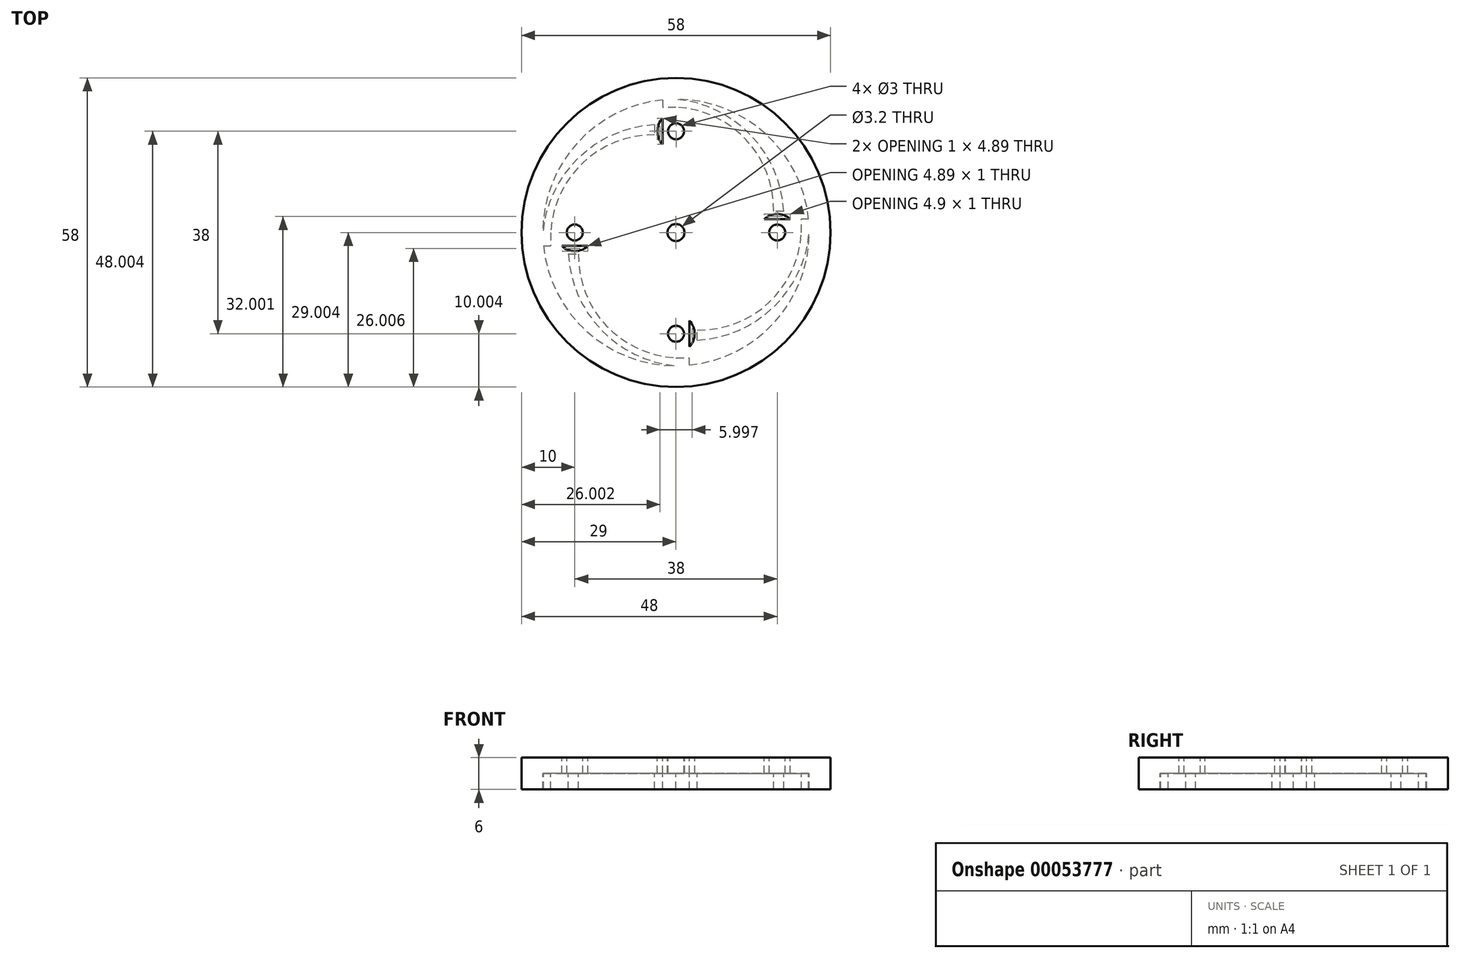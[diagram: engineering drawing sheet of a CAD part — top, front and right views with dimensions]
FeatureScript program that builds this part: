
annotation { "Feature Type Name" : "Feature", "Feature Type Description" : "" }
export const myFeature = defineFeature(function(context is Context, id is Id, definition is map)
    precondition{}
    {
        {
            var Q0;
            Q0=qCreatedBy(makeId("Top.planeOp"),FACE);
            var sketch = newSketch(context, id + "F0", { "sketchPlane" : qUnion([Q0])});
            skCircle(sketch, "E0", {"center": v(0, -6.1) * mm, "radius": 1.6 * mm});
            skCircle(sketch, "E1", {"center": v(0, -6.1) * mm, "radius": 25 * mm});
            skCircle(sketch, "E2", {"center": v(0, -6.1) * mm, "radius": 29 * mm});
            skLineSegment(sketch, "E3", {"start": v(-25, -6.1) * mm, "end": v(25, -6.1) * mm, "construction": true});
            skLineSegment(sketch, "E4", {"start": v(0, 18.9) * mm, "end": v(0, -31.1) * mm, "construction": true});
            skLineSegment(sketch, "E5", {"start": v(0, 13.94) * mm, "end": v(0, 11.74) * mm, "construction": true});
            skLineSegment(sketch, "E6", {"start": v(0, 11.74) * mm, "end": v(0, 13.94) * mm, "construction": true});
            skPoint(sketch, "E7", {"position": v(-23.5, -6.1) * mm});
            skArc(sketch, "E8", {"start": v(-4, 14.1) * mm, "mid": v(-18.27, 7.91) * mm, "end": v(-25, -6.1) * mm});
            skArc(sketch, "E9", {"start": v(-4, 12.22) * mm, "mid": v(-17.46, 7) * mm, "end": v(-23.5, -6.1) * mm});
            skLineSegment(sketch, "E10", {"start": v(-25, -6.1) * mm, "end": v(-23.5, -6.1) * mm});
            skLineSegment(sketch, "E11", {"start": v(-4, 14.1) * mm, "end": v(-4, 12.22) * mm});
            skLineSegment(sketch, "E12.1.0", {"start": v(-20.2, -10.1) * mm, "end": v(-18.33, -10.1) * mm});
            skArc(sketch, "E12.1.1", {"start": v(-20.2, -10.1) * mm, "mid": v(-14.02, -24.38) * mm, "end": v(0, -31.1) * mm});
            skArc(sketch, "E12.1.2", {"start": v(-18.33, -10.1) * mm, "mid": v(-13.1, -23.56) * mm, "end": v(0, -29.6) * mm});
            skLineSegment(sketch, "E12.1.3", {"start": v(0, -31.1) * mm, "end": v(0, -29.6) * mm});
            skLineSegment(sketch, "E12.2.0", {"start": v(4, -26.3) * mm, "end": v(4, -24.43) * mm});
            skArc(sketch, "E12.2.1", {"start": v(4, -26.3) * mm, "mid": v(18.27, -20.13) * mm, "end": v(25, -6.1) * mm});
            skArc(sketch, "E12.2.2", {"start": v(4, -24.43) * mm, "mid": v(17.46, -19.21) * mm, "end": v(23.5, -6.1) * mm});
            skLineSegment(sketch, "E12.2.3", {"start": v(25, -6.1) * mm, "end": v(23.5, -6.1) * mm});
            skLineSegment(sketch, "E12.3.0", {"start": v(20.2, -2.1) * mm, "end": v(18.33, -2.1) * mm});
            skArc(sketch, "E12.3.1", {"start": v(20.2, -2.1) * mm, "mid": v(14.02, 12.16) * mm, "end": v(0, 18.9) * mm});
            skArc(sketch, "E12.3.2", {"start": v(18.33, -2.1) * mm, "mid": v(13.1, 11.35) * mm, "end": v(0, 17.4) * mm});
            skLineSegment(sketch, "E12.3.3", {"start": v(0, 18.9) * mm, "end": v(0, 17.4) * mm});
            skLineSegment(sketch, "E13", {"start": v(-2.5, 18.77) * mm, "end": v(-2.5, -3.6) * mm});
            skLineSegment(sketch, "E14", {"start": v(2.5, -30.98) * mm, "end": v(2.5, -8.6) * mm});
            skLineSegment(sketch, "E15", {"start": v(-24.87, -8.6) * mm, "end": v(-2.5, -8.6) * mm});
            skLineSegment(sketch, "E16", {"start": v(24.88, -3.6) * mm, "end": v(2.5, -3.6) * mm});
            skPoint(sketch, "E17", {"position": v(2.5, -8.6) * mm});
            skPoint(sketch, "E18", {"position": v(2.5, -3.6) * mm});
            skPoint(sketch, "E19", {"position": v(-2.5, -3.6) * mm});
            skPoint(sketch, "E20", {"position": v(-2.5, -8.6) * mm});
            skLineSegment(sketch, "E21.trimOffspring", {"start": v(2.5, -8.6) * mm, "end": v(23.22, -8.6) * mm});
            skLineSegment(sketch, "E22.trimOffspring", {"start": v(-2.5, -8.6) * mm, "end": v(-2.5, -29.32) * mm});
            skLineSegment(sketch, "E23.trimOffspring", {"start": v(2.5, -3.6) * mm, "end": v(2.5, 17.11) * mm});
            skLineSegment(sketch, "E24.trimOffspring", {"start": v(-2.5, -3.6) * mm, "end": v(-23.22, -3.6) * mm});
            skLineSegment(sketch, "E25", {"start": v(23.5, -6.1) * mm, "end": v(23.5, -3.6) * mm});
            skLineSegment(sketch, "E26", {"start": v(0, 17.4) * mm, "end": v(-2.5, 17.4) * mm});
            skLineSegment(sketch, "E27", {"start": v(-23.5, -6.1) * mm, "end": v(-23.5, -8.6) * mm});
            skLineSegment(sketch, "E28", {"start": v(0, -29.6) * mm, "end": v(2.5, -29.6) * mm});
            skCircle(sketch, "E29", {"center": v(19, -6.1) * mm, "radius": 1.5 * mm});
            skCircle(sketch, "E30.1.0", {"center": v(0, 12.9) * mm, "radius": 1.5 * mm});
            skCircle(sketch, "E30.2.0", {"center": v(-19, -6.1) * mm, "radius": 1.5 * mm});
            skCircle(sketch, "E30.3.0", {"center": v(0, -25.1) * mm, "radius": 1.5 * mm});
            skCircle(sketch, "E31", {"center": v(-19, -6.1) * mm, "radius": 3.5 * mm});
            skCircle(sketch, "E32.1.0", {"center": v(0, -25.1) * mm, "radius": 3.5 * mm});
            skCircle(sketch, "E32.2.0", {"center": v(19, -6.1) * mm, "radius": 3.5 * mm});
            skCircle(sketch, "E32.3.0", {"center": v(0, 12.9) * mm, "radius": 3.5 * mm});
            skSolve(sketch);
        }
        {
            var Q0;
            Q0=makeQuery(id+"F0.imprint","IMPRINT",FACE,{"disambiguationData":[TD([[makeQuery(id+"F0.imprint","IMPRINT",EDGE,{"derivedFrom":sQuery(id+"F0.wireOp",EDGE,"E0")}),-1.0]])]});
            var Q1;
            {var subQ0=sQuery(id+"F0.wireOp",EDGE,"E31");var subQ1=sQuery(id+"F0.wireOp",EDGE,"E15");var subQ2=makeQuery(id+"F0.imprint","INTERSECT",VERTEX,{"disambiguationData":[OD(0.0)],"derivedFrom":[subQ1,subQ0]});Q1=makeQuery(id+"F0.imprint","IMPRINT",FACE,{"disambiguationData":[TD([[makeQuery(id+"F0.imprint","IMPRINT",EDGE,{"disambiguationData":[TD([[subQ2,-1.0]])],"derivedFrom":subQ1}),-1.0]])]});}
            var Q2;
            {var subQ0=sQuery(id+"F0.wireOp",EDGE,"E31");var subQ1=sQuery(id+"F0.wireOp",EDGE,"E24.trimOffspring");var subQ2=makeQuery(id+"F0.imprint","INTERSECT",VERTEX,{"disambiguationData":[OD(0.0)],"derivedFrom":[subQ1,subQ0]});Q2=makeQuery(id+"F0.imprint","IMPRINT",FACE,{"disambiguationData":[TD([[makeQuery(id+"F0.imprint","IMPRINT",EDGE,{"disambiguationData":[TD([[subQ2,-1.0]])],"derivedFrom":subQ1}),-1.0]])]});}
            var Q3;
            Q3=makeQuery(id+"F0.imprint","IMPRINT",FACE,{"disambiguationData":[TD([[makeQuery(id+"F0.imprint","IMPRINT",EDGE,{"derivedFrom":sQuery(id+"F0.wireOp",EDGE,"E30.2.0")}),-1.0]])]});
            var Q4;
            {var subQ0=sQuery(id+"F0.wireOp",EDGE,"E27");Q4=makeQuery(id+"F0.imprint","IMPRINT",FACE,{"disambiguationData":[TD([[makeQuery(id+"F0.imprint","IMPRINT",EDGE,{"derivedFrom":subQ0}),1.0]])]});}
            var Q5;
            {var subQ5=sQuery(id+"F0.wireOp",EDGE,"E26");Q5=makeQuery(id+"F0.imprint","IMPRINT",FACE,{"disambiguationData":[TD([[makeQuery(id+"F0.imprint","IMPRINT",EDGE,{"derivedFrom":subQ5}),1.0]])]});}
            var Q6;
            {var subQ0=sQuery(id+"F0.wireOp",EDGE,"E32.3.0");var subQ1=sQuery(id+"F0.wireOp",EDGE,"E13");var subQ2=makeQuery(id+"F0.imprint","INTERSECT",VERTEX,{"disambiguationData":[OD(0.0)],"derivedFrom":[subQ1,subQ0]});Q6=makeQuery(id+"F0.imprint","IMPRINT",FACE,{"disambiguationData":[TD([[makeQuery(id+"F0.imprint","IMPRINT",EDGE,{"disambiguationData":[TD([[subQ2,-1.0]])],"derivedFrom":subQ1}),-1.0]])]});}
            var Q7;
            Q7=makeQuery(id+"F0.imprint","IMPRINT",FACE,{"disambiguationData":[TD([[makeQuery(id+"F0.imprint","IMPRINT",EDGE,{"derivedFrom":sQuery(id+"F0.wireOp",EDGE,"E30.1.0")}),-1.0]])]});
            var Q8;
            {var subQ0=sQuery(id+"F0.wireOp",EDGE,"E32.3.0");var subQ1=sQuery(id+"F0.wireOp",EDGE,"E23.trimOffspring");var subQ2=makeQuery(id+"F0.imprint","INTERSECT",VERTEX,{"disambiguationData":[OD(0.0)],"derivedFrom":[subQ1,subQ0]});Q8=makeQuery(id+"F0.imprint","IMPRINT",FACE,{"disambiguationData":[TD([[makeQuery(id+"F0.imprint","IMPRINT",EDGE,{"disambiguationData":[TD([[subQ2,-1.0]])],"derivedFrom":subQ1}),-1.0]])]});}
            var Q9;
            Q9=makeQuery(id+"F0.imprint","IMPRINT",FACE,{"disambiguationData":[TD([[makeQuery(id+"F0.imprint","IMPRINT",EDGE,{"derivedFrom":sQuery(id+"F0.wireOp",EDGE,"E29")}),-1.0]])]});
            var Q10;
            {var subQ0=sQuery(id+"F0.wireOp",EDGE,"E25");Q10=makeQuery(id+"F0.imprint","IMPRINT",FACE,{"disambiguationData":[TD([[makeQuery(id+"F0.imprint","IMPRINT",EDGE,{"derivedFrom":subQ0}),1.0]])]});}
            var Q11;
            {var subQ0=sQuery(id+"F0.wireOp",EDGE,"E32.2.0");var subQ1=sQuery(id+"F0.wireOp",EDGE,"E21.trimOffspring");var subQ2=makeQuery(id+"F0.imprint","INTERSECT",VERTEX,{"disambiguationData":[OD(0.0)],"derivedFrom":[subQ1,subQ0]});Q11=makeQuery(id+"F0.imprint","IMPRINT",FACE,{"disambiguationData":[TD([[makeQuery(id+"F0.imprint","IMPRINT",EDGE,{"disambiguationData":[TD([[subQ2,-1.0]])],"derivedFrom":subQ1}),-1.0]])]});}
            var Q12;
            {var subQ0=sQuery(id+"F0.wireOp",EDGE,"E32.2.0");var subQ1=sQuery(id+"F0.wireOp",EDGE,"E16");var subQ2=makeQuery(id+"F0.imprint","INTERSECT",VERTEX,{"disambiguationData":[OD(0.0)],"derivedFrom":[subQ1,subQ0]});Q12=makeQuery(id+"F0.imprint","IMPRINT",FACE,{"disambiguationData":[TD([[makeQuery(id+"F0.imprint","IMPRINT",EDGE,{"disambiguationData":[TD([[subQ2,-1.0]])],"derivedFrom":subQ1}),-1.0]])]});}
            var Q13;
            Q13=makeQuery(id+"F0.imprint","IMPRINT",FACE,{"disambiguationData":[TD([[makeQuery(id+"F0.imprint","IMPRINT",EDGE,{"derivedFrom":sQuery(id+"F0.wireOp",EDGE,"E30.3.0")}),-1.0]])]});
            var Q14;
            {var subQ0=sQuery(id+"F0.wireOp",EDGE,"E28");Q14=makeQuery(id+"F0.imprint","IMPRINT",FACE,{"disambiguationData":[TD([[makeQuery(id+"F0.imprint","IMPRINT",EDGE,{"derivedFrom":subQ0}),1.0]])]});}
            var Q15;
            {var subQ0=sQuery(id+"F0.wireOp",EDGE,"E32.1.0");var subQ1=sQuery(id+"F0.wireOp",EDGE,"E22.trimOffspring");var subQ2=makeQuery(id+"F0.imprint","INTERSECT",VERTEX,{"disambiguationData":[OD(0.0)],"derivedFrom":[subQ1,subQ0]});Q15=makeQuery(id+"F0.imprint","IMPRINT",FACE,{"disambiguationData":[TD([[makeQuery(id+"F0.imprint","IMPRINT",EDGE,{"disambiguationData":[TD([[subQ2,-1.0]])],"derivedFrom":subQ1}),-1.0]])]});}
            var Q16;
            {var subQ0=sQuery(id+"F0.wireOp",EDGE,"E32.1.0");var subQ1=sQuery(id+"F0.wireOp",EDGE,"E14");var subQ2=makeQuery(id+"F0.imprint","INTERSECT",VERTEX,{"disambiguationData":[OD(0.0)],"derivedFrom":[subQ1,subQ0]});Q16=makeQuery(id+"F0.imprint","IMPRINT",FACE,{"disambiguationData":[TD([[makeQuery(id+"F0.imprint","IMPRINT",EDGE,{"disambiguationData":[TD([[subQ2,-1.0]])],"derivedFrom":subQ1}),-1.0]])]});}
            extrude(context, id + "F1", {"entities" : qUnion([Q0, Q1, Q2, Q3, Q4, Q5, Q6, Q7, Q8, Q9, Q10, Q11, Q12, Q13, Q14, Q15, Q16]), "oppositeDirection" : true, "depth" : 3 * mm});
        }
        {
            var Q0;
            {var subQ0=sQuery(id+"F0.wireOp",EDGE,"E10");Q0=makeQuery(id+"F0.imprint","IMPRINT",FACE,{"disambiguationData":[TD([[makeQuery(id+"F0.imprint","IMPRINT",EDGE,{"derivedFrom":subQ0}),-1.0]])]});}
            var Q1;
            {var subQ0=sQuery(id+"F0.wireOp",EDGE,"E12.1.3");Q1=makeQuery(id+"F0.imprint","IMPRINT",FACE,{"disambiguationData":[TD([[makeQuery(id+"F0.imprint","IMPRINT",EDGE,{"derivedFrom":subQ0}),-1.0]])]});}
            var Q2;
            {var subQ0=sQuery(id+"F0.wireOp",EDGE,"E12.2.3");Q2=makeQuery(id+"F0.imprint","IMPRINT",FACE,{"disambiguationData":[TD([[makeQuery(id+"F0.imprint","IMPRINT",EDGE,{"derivedFrom":subQ0}),-1.0]])]});}
            var Q3;
            {var subQ0=sQuery(id+"F0.wireOp",EDGE,"E12.3.3");Q3=makeQuery(id+"F0.imprint","IMPRINT",FACE,{"disambiguationData":[TD([[makeQuery(id+"F0.imprint","IMPRINT",EDGE,{"derivedFrom":subQ0}),-1.0]])]});}
            var Q4;
            Q4=makeQuery(id+"F0.imprint","IMPRINT",FACE,{"disambiguationData":[TD([[makeQuery(id+"F0.imprint","IMPRINT",EDGE,{"derivedFrom":sQuery(id+"F0.wireOp",EDGE,"E2")}),1.0]])]});
            var Q5;
            {var subQ0=sQuery(id+"F0.wireOp",EDGE,"E10");Q5=makeQuery(id+"F0.imprint","IMPRINT",FACE,{"disambiguationData":[TD([[makeQuery(id+"F0.imprint","IMPRINT",EDGE,{"derivedFrom":subQ0}),1.0]])]});}
            var Q6;
            {var subQ3=sQuery(id+"F0.wireOp",EDGE,"E12.3.0");Q6=makeQuery(id+"F0.imprint","IMPRINT",FACE,{"disambiguationData":[TD([[makeQuery(id+"F0.imprint","IMPRINT",EDGE,{"derivedFrom":subQ3}),-1.0]])]});}
            var Q7;
            {var subQ3=sQuery(id+"F0.wireOp",EDGE,"E12.1.0");Q7=makeQuery(id+"F0.imprint","IMPRINT",FACE,{"disambiguationData":[TD([[makeQuery(id+"F0.imprint","IMPRINT",EDGE,{"derivedFrom":subQ3}),-1.0]])]});}
            var Q8;
            {var subQ3=sQuery(id+"F0.wireOp",EDGE,"E12.2.0");Q8=makeQuery(id+"F0.imprint","IMPRINT",FACE,{"disambiguationData":[TD([[makeQuery(id+"F0.imprint","IMPRINT",EDGE,{"derivedFrom":subQ3}),-1.0]])]});}
            extrude(context, id + "F2", {"entities" : qUnion([Q0, Q1, Q2, Q3, Q4, Q5, Q6, Q7, Q8]), "operationType" : NewBodyOperationType.ADD, "oppositeDirection" : true, "depth" : 6 * mm});
        }
    });
